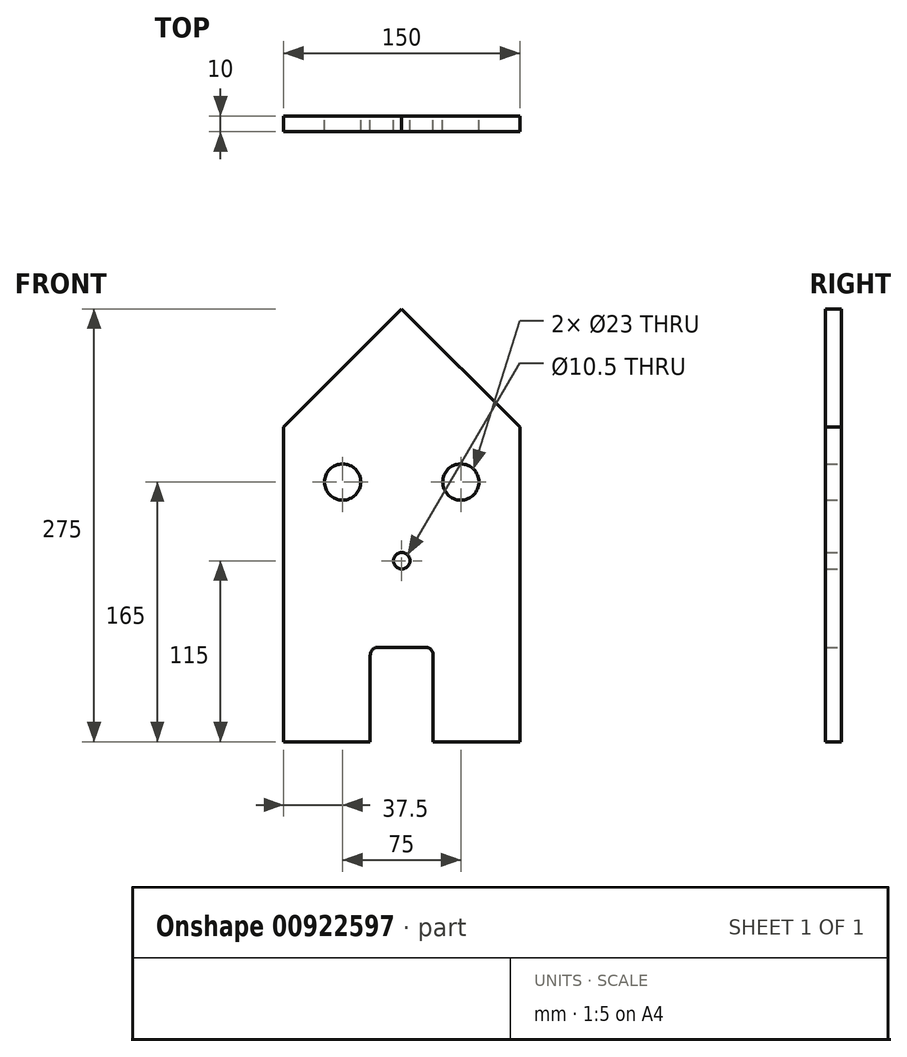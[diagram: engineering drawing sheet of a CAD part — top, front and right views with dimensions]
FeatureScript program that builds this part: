
annotation { "Feature Type Name" : "Feature", "Feature Type Description" : "" }
export const myFeature = defineFeature(function(context is Context, id is Id, definition is map)
    precondition{}
    {
        {
            var Q0;
            Q0=qCreatedBy(makeId("Front.planeOp"),FACE);
            var sketch = newSketch(context, id + "F0", { "sketchPlane" : qUnion([Q0])});
            skLineSegment(sketch, "E0.bottom", {"start": v(75, 100) * mm, "end": v(-75, 100) * mm});
            skLineSegment(sketch, "E0.top", {"start": v(75, -100) * mm, "end": v(-75, -100) * mm, "construction": true});
            skLineSegment(sketch, "E0.left", {"start": v(75, 100) * mm, "end": v(75, -100) * mm});
            skLineSegment(sketch, "E0.right", {"start": v(-75, 100) * mm, "end": v(-75, -100) * mm});
            skPoint(sketch, "E0.middle", {"position": v(0, 0) * mm});
            skLineSegment(sketch, "E1", {"start": v(0, 100) * mm, "end": v(0, 175) * mm});
            skLineSegment(sketch, "E2", {"start": v(0, 175) * mm, "end": v(-75, 100) * mm});
            skLineSegment(sketch, "E3", {"start": v(0, 175) * mm, "end": v(75, 100) * mm});
            skLineSegment(sketch, "E4", {"start": v(0, -100) * mm, "end": v(0, -40) * mm, "construction": true});
            skLineSegment(sketch, "E5", {"start": v(-20, -40) * mm, "end": v(20, -40) * mm});
            skLineSegment(sketch, "E6", {"start": v(-20, -40) * mm, "end": v(-20, -100) * mm});
            skLineSegment(sketch, "E7", {"start": v(20, -40) * mm, "end": v(20, -100) * mm});
            skLineSegment(sketch, "E8", {"start": v(20, -100) * mm, "end": v(75, -100) * mm});
            skLineSegment(sketch, "E9", {"start": v(-20, -100) * mm, "end": v(-75, -100) * mm});
            skCircle(sketch, "E10", {"center": v(37.5, 65) * mm, "radius": 11.5 * mm});
            skLineSegment(sketch, "E11", {"start": v(-75, 65) * mm, "end": v(75, 65) * mm, "construction": true});
            skCircle(sketch, "E12.MirrorC", {"center": v(-37.5, 65) * mm, "radius": 11.5 * mm});
            skSolve(sketch);
        }
        {
            var Q0;
            Q0 = qSketchRegion(id + "F0", true);
            extrude(context, id + "F1", {"entities" : qUnion([Q0]), "depth" : 10 * mm, "offsetDistance" : 25.4 * mm});
        }
        {
            var Q0;
            Q0=makeQuery(id+"F1.opExtrude","SWEPT_EDGE",EDGE,{"disambiguationData":[OSD([sQuery(id+"F0.wireOp",EDGE,"E5"),sQuery(id+"F0.wireOp",EDGE,"E6")])]});
            var Q1;
            Q1=makeQuery(id+"F1.opExtrude","SWEPT_EDGE",EDGE,{"disambiguationData":[OSD([sQuery(id+"F0.wireOp",EDGE,"E5"),sQuery(id+"F0.wireOp",EDGE,"E7")])]});
            fillet(context, id + "F2", {"entities" : qUnion([Q0, Q1]), "radius" : 5 * mm, "tangentPropagation" : true, "allowEdgeOverflow" : false});
        }
        {
            var Q0;
            Q0=makeQuery(id+"F1.opExtrude","CAP_FACE",FACE,{"disambiguationData":[OSD([sQuery(id+"F0.wireOp",EDGE,"E0.left"),sQuery(id+"F0.wireOp",EDGE,"E0.right"),sQuery(id+"F0.wireOp",EDGE,"E2"),sQuery(id+"F0.wireOp",EDGE,"E3"),sQuery(id+"F0.wireOp",EDGE,"E5"),sQuery(id+"F0.wireOp",EDGE,"E6"),sQuery(id+"F0.wireOp",EDGE,"E7"),sQuery(id+"F0.wireOp",EDGE,"E8"),sQuery(id+"F0.wireOp",EDGE,"E9"),sQuery(id+"F0.wireOp",EDGE,"E10"),sQuery(id+"F0.wireOp",EDGE,"E12.MirrorC")])],"isStart":true});
            var sketch = newSketch(context, id + "F3", { "sketchPlane" : qUnion([Q0])});
            skCircle(sketch, "E13", {"center": v(0, 15) * mm, "radius": 5.25 * mm});
            skSolve(sketch);
        }
        {
            var Q0;
            Q0 = qSketchRegion(id + "F3", true);
            extrude(context, id + "F4", {"entities" : qUnion([Q0]), "operationType" : NewBodyOperationType.REMOVE, "endBound" : BoundingType.THROUGH_ALL, "oppositeDirection" : true, "depth" : 25.4 * mm, "offsetDistance" : 25.4 * mm});
        }
    });
